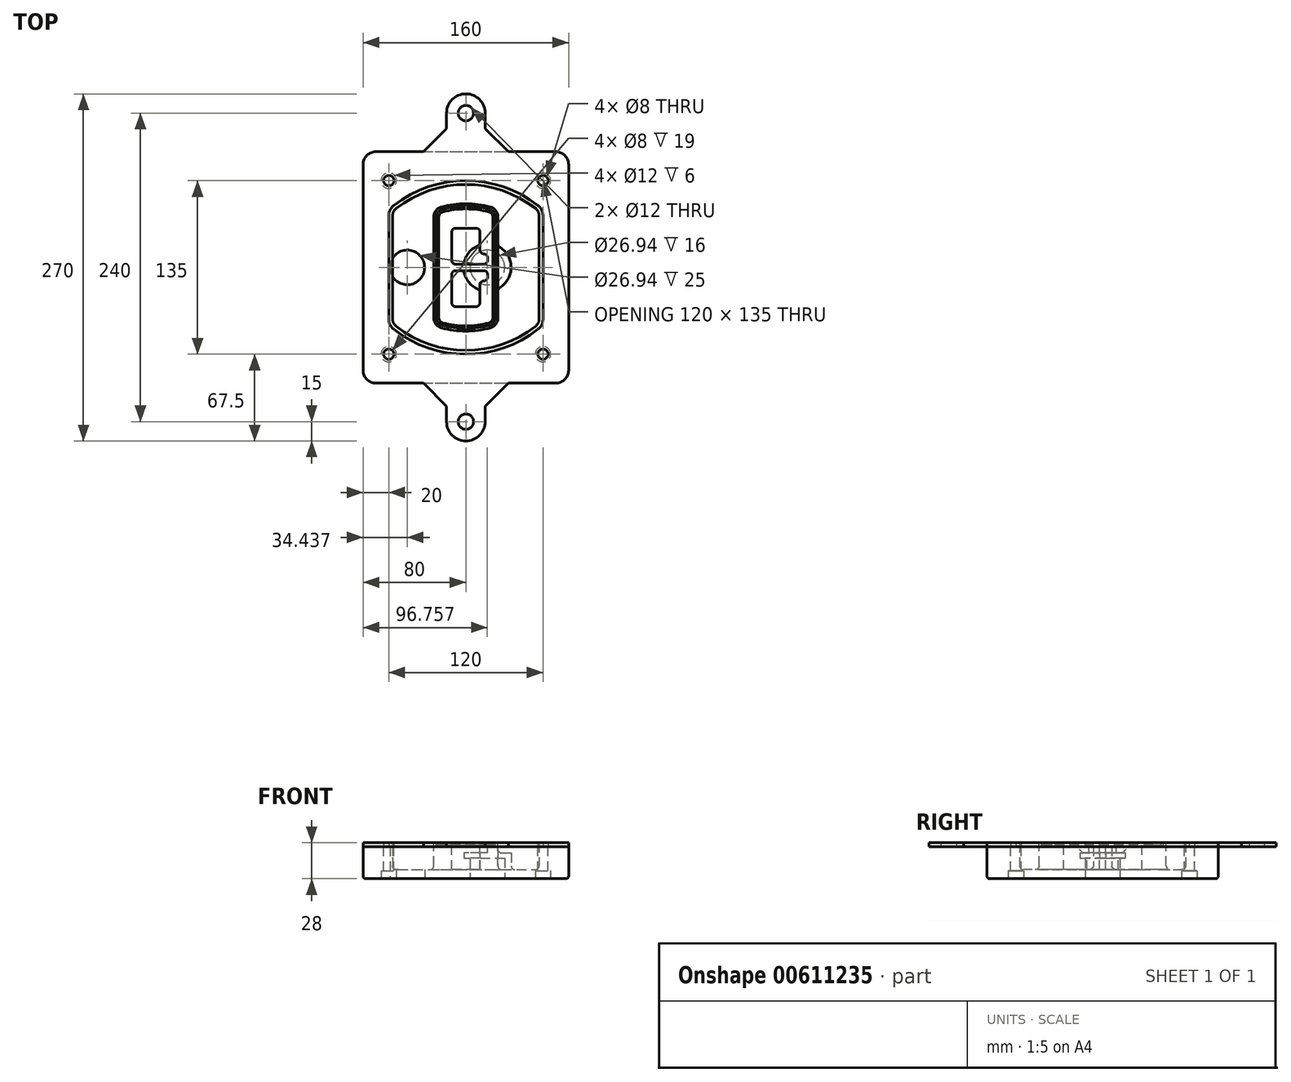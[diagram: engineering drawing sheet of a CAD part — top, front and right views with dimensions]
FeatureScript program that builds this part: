
annotation { "Feature Type Name" : "Feature", "Feature Type Description" : "" }
export const myFeature = defineFeature(function(context is Context, id is Id, definition is map)
    precondition{}
    {
        {
            var Q0;
            Q0=qCreatedBy(makeId("Top.planeOp"),FACE);
            var sketch = newSketch(context, id + "F0", { "sketchPlane" : qUnion([Q0])});
            skPoint(sketch, "E0.rect.middle", {"position": v(0, 0) * mm});
            skLineSegment(sketch, "E1.bottom", {"start": v(-70, -90) * mm, "end": v(70, -90) * mm});
            skLineSegment(sketch, "E1.top", {"start": v(-70, 90) * mm, "end": v(70, 90) * mm});
            skLineSegment(sketch, "E1.left", {"start": v(-80, -80) * mm, "end": v(-80, 80) * mm});
            skLineSegment(sketch, "E1.right", {"start": v(80, -80) * mm, "end": v(80, 80) * mm});
            skLineSegment(sketch, "E2", {"start": v(-80, 90) * mm, "end": v(80, -90) * mm, "construction": true});
            skLineSegment(sketch, "E3", {"start": v(80, 90) * mm, "end": v(-80, -90) * mm, "construction": true});
            skCircle(sketch, "E4", {"center": v(-60, 67.5) * mm, "radius": 4 * mm});
            skCircle(sketch, "E5", {"center": v(60, 67.5) * mm, "radius": 4 * mm});
            skCircle(sketch, "E6", {"center": v(60, -67.5) * mm, "radius": 4 * mm});
            skCircle(sketch, "E7", {"center": v(-60, -67.5) * mm, "radius": 4 * mm});
            skLineSegment(sketch, "E8", {"start": v(-60, 67.5) * mm, "end": v(60, 67.5) * mm, "construction": true});
            skLineSegment(sketch, "E9", {"start": v(60, 67.5) * mm, "end": v(60, -67.5) * mm, "construction": true});
            skLineSegment(sketch, "E10", {"start": v(60, -67.5) * mm, "end": v(-60, -67.5) * mm, "construction": true});
            skLineSegment(sketch, "E11", {"start": v(-60, -67.5) * mm, "end": v(-60, 67.5) * mm, "construction": true});
            skLineSegment(sketch, "E12", {"start": v(-60, 40.3) * mm, "end": v(-60, -40.3) * mm});
            skLineSegment(sketch, "E13", {"start": v(60, 40.3) * mm, "end": v(60, -40.3) * mm});
            skArc(sketch, "E14", {"start": v(56.15, 48.18) * mm, "mid": v(0, 67.5) * mm, "end": v(-56.15, 48.18) * mm});
            skArc(sketch, "E15", {"start": v(-56.15, -48.18) * mm, "mid": v(0, -67.5) * mm, "end": v(56.15, -48.18) * mm});
            skLineSegment(sketch, "E16", {"start": v(-60, 0) * mm, "end": v(60, 0) * mm, "construction": true});
            skPoint(sketch, "E17.visualSharp", {"position": v(-60, -45) * mm});
            skArc(sketch, "E17.filletArc", {"start": v(-60, -40.3) * mm, "mid": v(-58.99, -44.68) * mm, "end": v(-56.15, -48.18) * mm});
            skPoint(sketch, "E18.visualSharp", {"position": v(-60, 45) * mm});
            skArc(sketch, "E18.filletArc", {"start": v(-56.15, 48.18) * mm, "mid": v(-58.99, 44.68) * mm, "end": v(-60, 40.3) * mm});
            skPoint(sketch, "E19.visualSharp", {"position": v(60, 45) * mm});
            skArc(sketch, "E19.filletArc", {"start": v(60, 40.3) * mm, "mid": v(58.99, 44.68) * mm, "end": v(56.15, 48.18) * mm});
            skPoint(sketch, "E20.visualSharp", {"position": v(60, -45) * mm});
            skArc(sketch, "E20.filletArc", {"start": v(56.15, -48.18) * mm, "mid": v(58.99, -44.68) * mm, "end": v(60, -40.3) * mm});
            skPoint(sketch, "E21.visualSharp", {"position": v(-80, 90) * mm});
            skArc(sketch, "E21.filletArc", {"start": v(-70, 90) * mm, "mid": v(-77.07, 87.07) * mm, "end": v(-80, 80) * mm});
            skPoint(sketch, "E22.visualSharp", {"position": v(80, 90) * mm});
            skArc(sketch, "E22.filletArc", {"start": v(80, 80) * mm, "mid": v(77.07, 87.07) * mm, "end": v(70, 90) * mm});
            skPoint(sketch, "E23.visualSharp", {"position": v(80, -90) * mm});
            skArc(sketch, "E23.filletArc", {"start": v(70, -90) * mm, "mid": v(77.07, -87.07) * mm, "end": v(80, -80) * mm});
            skPoint(sketch, "E24.visualSharp", {"position": v(-80, -90) * mm});
            skArc(sketch, "E24.filletArc", {"start": v(-80, -80) * mm, "mid": v(-77.07, -87.07) * mm, "end": v(-70, -90) * mm});
            skArc(sketch, "E25.0", {"start": v(57, 40.3) * mm, "mid": v(56.3, 43.36) * mm, "end": v(54.3, 45.81) * mm});
            skLineSegment(sketch, "E25.1", {"start": v(57, 40.3) * mm, "end": v(57, -40.3) * mm});
            skArc(sketch, "E25.2", {"start": v(54.3, -45.81) * mm, "mid": v(56.3, -43.36) * mm, "end": v(57, -40.3) * mm});
            skArc(sketch, "E25.3", {"start": v(-54.3, -45.81) * mm, "mid": v(0, -64.5) * mm, "end": v(54.3, -45.81) * mm});
            skArc(sketch, "E25.4", {"start": v(-57, -40.3) * mm, "mid": v(-56.3, -43.36) * mm, "end": v(-54.3, -45.81) * mm});
            skArc(sketch, "E25.5", {"start": v(54.3, 45.81) * mm, "mid": v(0, 64.5) * mm, "end": v(-54.3, 45.81) * mm});
            skLineSegment(sketch, "E25.6", {"start": v(-57, 40.3) * mm, "end": v(-57, -40.3) * mm});
            skArc(sketch, "E25.7", {"start": v(-54.3, 45.81) * mm, "mid": v(-56.3, 43.36) * mm, "end": v(-57, 40.3) * mm});
            skArc(sketch, "E26.0", {"start": v(-58.62, 51.33) * mm, "mid": v(-62.58, 46.43) * mm, "end": v(-64, 40.3) * mm});
            skArc(sketch, "E26.1", {"start": v(58.62, 51.33) * mm, "mid": v(0, 71.5) * mm, "end": v(-58.62, 51.33) * mm});
            skArc(sketch, "E26.2", {"start": v(64, 40.3) * mm, "mid": v(62.58, 46.43) * mm, "end": v(58.62, 51.33) * mm});
            skLineSegment(sketch, "E26.3", {"start": v(64, 40.3) * mm, "end": v(64, -40.3) * mm});
            skArc(sketch, "E26.4", {"start": v(58.62, -51.33) * mm, "mid": v(62.58, -46.43) * mm, "end": v(64, -40.3) * mm});
            skLineSegment(sketch, "E26.5", {"start": v(-64, 40.3) * mm, "end": v(-64, -40.3) * mm});
            skArc(sketch, "E26.6", {"start": v(-58.62, -51.33) * mm, "mid": v(0, -71.5) * mm, "end": v(58.62, -51.33) * mm});
            skArc(sketch, "E26.7", {"start": v(-64, -40.3) * mm, "mid": v(-62.58, -46.43) * mm, "end": v(-58.62, -51.33) * mm});
            skSolve(sketch);
        }
        {
            var Q0;
            Q0=makeQuery(id+"F0.imprint","IMPRINT",FACE,{"disambiguationData":[TD([[makeQuery(id+"F0.imprint","IMPRINT",EDGE,{"derivedFrom":sQuery(id+"F0.wireOp",EDGE,"E1.bottom")}),1.0]])]});
            var Q1;
            Q1=makeQuery(id+"F0.imprint","IMPRINT",FACE,{"disambiguationData":[TD([[makeQuery(id+"F0.imprint","IMPRINT",EDGE,{"derivedFrom":sQuery(id+"F0.wireOp",EDGE,"E12")}),1.0]])]});
            var Q2;
            Q2=makeQuery(id+"F0.imprint","IMPRINT",FACE,{"disambiguationData":[TD([[makeQuery(id+"F0.imprint","IMPRINT",EDGE,{"derivedFrom":sQuery(id+"F0.wireOp",EDGE,"E25.0")}),1.0]])]});
            var Q3;
            Q3=makeQuery(id+"F0.imprint","IMPRINT",FACE,{"disambiguationData":[TD([[makeQuery(id+"F0.imprint","IMPRINT",EDGE,{"derivedFrom":sQuery(id+"F0.wireOp",EDGE,"E12")}),-1.0]])]});
            extrude(context, id + "F1", {"entities" : qUnion([Q0, Q1, Q2, Q3]), "oppositeDirection" : true, "depth" : 25 * mm});
        }
        {
            var Q0;
            Q0=makeQuery(id+"F0.imprint","IMPRINT",FACE,{"disambiguationData":[TD([[makeQuery(id+"F0.imprint","IMPRINT",EDGE,{"derivedFrom":sQuery(id+"F0.wireOp",EDGE,"E12")}),1.0]])]});
            extrude(context, id + "F2", {"entities" : qUnion([Q0]), "operationType" : NewBodyOperationType.ADD, "depth" : 3 * mm});
        }
        {
            var Q0;
            Q0=makeQuery(id+"F0.imprint","IMPRINT",FACE,{"disambiguationData":[TD([[makeQuery(id+"F0.imprint","IMPRINT",EDGE,{"derivedFrom":sQuery(id+"F0.wireOp",EDGE,"E25.0")}),1.0]])]});
            extrude(context, id + "F3", {"entities" : qUnion([Q0]), "operationType" : NewBodyOperationType.REMOVE, "oppositeDirection" : true, "depth" : 18 * mm});
        }
        {
            var Q0;
            Q0=makeQuery(id+"F2.opExtrude","CAP_FACE",FACE,{"disambiguationData":[OSD([sQuery(id+"F0.wireOp",EDGE,"E12"),sQuery(id+"F0.wireOp",EDGE,"E13"),sQuery(id+"F0.wireOp",EDGE,"E14"),sQuery(id+"F0.wireOp",EDGE,"E15"),sQuery(id+"F0.wireOp",EDGE,"E17.filletArc"),sQuery(id+"F0.wireOp",EDGE,"E18.filletArc"),sQuery(id+"F0.wireOp",EDGE,"E19.filletArc"),sQuery(id+"F0.wireOp",EDGE,"E20.filletArc"),sQuery(id+"F0.wireOp",EDGE,"E25.0"),sQuery(id+"F0.wireOp",EDGE,"E25.1"),sQuery(id+"F0.wireOp",EDGE,"E25.2"),sQuery(id+"F0.wireOp",EDGE,"E25.3"),sQuery(id+"F0.wireOp",EDGE,"E25.4"),sQuery(id+"F0.wireOp",EDGE,"E25.5"),sQuery(id+"F0.wireOp",EDGE,"E25.6"),sQuery(id+"F0.wireOp",EDGE,"E25.7")])],"isStart":false});
            var sketch = newSketch(context, id + "F4", { "sketchPlane" : qUnion([Q0])});
            skArc(sketch, "E27.0", {"start": v(-19.08, -46.97) * mm, "mid": v(0, -49.5) * mm, "end": v(19.08, -46.97) * mm});
            skArc(sketch, "E28.0", {"start": v(19.08, 46.97) * mm, "mid": v(0, 49.5) * mm, "end": v(-19.08, 46.97) * mm});
            skLineSegment(sketch, "E29", {"start": v(-25, 39.25) * mm, "end": v(-25, -39.25) * mm});
            skLineSegment(sketch, "E30", {"start": v(25, 39.25) * mm, "end": v(25, -39.25) * mm});
            skLineSegment(sketch, "E31", {"start": v(-25, 45.1) * mm, "end": v(25, 45.1) * mm, "construction": true});
            skLineSegment(sketch, "E32", {"start": v(-25, -45.1) * mm, "end": v(25, -45.1) * mm, "construction": true});
            skPoint(sketch, "E33.visualSharp", {"position": v(-25, 45.1) * mm});
            skArc(sketch, "E33.filletArc", {"start": v(-19.08, 46.97) * mm, "mid": v(-23.35, 44.11) * mm, "end": v(-25, 39.25) * mm});
            skPoint(sketch, "E34.visualSharp", {"position": v(25, 45.1) * mm});
            skArc(sketch, "E34.filletArc", {"start": v(25, 39.25) * mm, "mid": v(23.35, 44.11) * mm, "end": v(19.08, 46.97) * mm});
            skPoint(sketch, "E35.visualSharp", {"position": v(25, -45.1) * mm});
            skArc(sketch, "E35.filletArc", {"start": v(19.08, -46.97) * mm, "mid": v(23.35, -44.11) * mm, "end": v(25, -39.25) * mm});
            skPoint(sketch, "E36.visualSharp", {"position": v(-25, -45.1) * mm});
            skArc(sketch, "E36.filletArc", {"start": v(-25, -39.25) * mm, "mid": v(-23.35, -44.11) * mm, "end": v(-19.08, -46.97) * mm});
            skArc(sketch, "E37.0", {"start": v(54.3, 45.81) * mm, "mid": v(0, 64.5) * mm, "end": v(-54.3, 45.81) * mm});
            skArc(sketch, "E37.1", {"start": v(-54.3, 45.81) * mm, "mid": v(-56.3, 43.36) * mm, "end": v(-57, 40.3) * mm});
            skLineSegment(sketch, "E37.2", {"start": v(-57, 40.3) * mm, "end": v(-57, -40.3) * mm});
            skArc(sketch, "E37.3", {"start": v(-57, -40.3) * mm, "mid": v(-56.3, -43.36) * mm, "end": v(-54.3, -45.81) * mm});
            skArc(sketch, "E37.4", {"start": v(-54.3, -45.81) * mm, "mid": v(0, -64.5) * mm, "end": v(54.3, -45.81) * mm});
            skArc(sketch, "E37.5", {"start": v(54.3, -45.81) * mm, "mid": v(56.3, -43.36) * mm, "end": v(57, -40.3) * mm});
            skLineSegment(sketch, "E37.6", {"start": v(57, 40.3) * mm, "end": v(57, -40.3) * mm});
            skArc(sketch, "E37.7", {"start": v(57, 40.3) * mm, "mid": v(56.3, 43.36) * mm, "end": v(54.3, 45.81) * mm});
            skLineSegment(sketch, "E38.0", {"start": v(23, 39.25) * mm, "end": v(23, -39.25) * mm});
            skArc(sketch, "E38.1", {"start": v(18.56, -45.04) * mm, "mid": v(21.76, -42.9) * mm, "end": v(23, -39.25) * mm});
            skArc(sketch, "E38.2", {"start": v(-18.56, -45.04) * mm, "mid": v(0, -47.5) * mm, "end": v(18.56, -45.04) * mm});
            skArc(sketch, "E38.3", {"start": v(-23, -39.25) * mm, "mid": v(-21.76, -42.9) * mm, "end": v(-18.56, -45.04) * mm});
            skLineSegment(sketch, "E38.4", {"start": v(-23, 39.25) * mm, "end": v(-23, -39.25) * mm});
            skArc(sketch, "E38.5", {"start": v(23, 39.25) * mm, "mid": v(21.76, 42.9) * mm, "end": v(18.56, 45.04) * mm});
            skArc(sketch, "E38.6", {"start": v(-18.56, 45.04) * mm, "mid": v(-21.76, 42.9) * mm, "end": v(-23, 39.25) * mm});
            skArc(sketch, "E38.7", {"start": v(18.56, 45.04) * mm, "mid": v(0, 47.5) * mm, "end": v(-18.56, 45.04) * mm});
            skArc(sketch, "E39.0", {"start": v(21, 39.25) * mm, "mid": v(20.18, 41.68) * mm, "end": v(18.04, 43.1) * mm});
            skLineSegment(sketch, "E39.1", {"start": v(21, 39.25) * mm, "end": v(21, -39.25) * mm});
            skArc(sketch, "E39.2", {"start": v(18.04, -43.1) * mm, "mid": v(20.18, -41.68) * mm, "end": v(21, -39.25) * mm});
            skArc(sketch, "E39.3", {"start": v(-18.04, -43.1) * mm, "mid": v(0, -45.5) * mm, "end": v(18.04, -43.1) * mm});
            skArc(sketch, "E39.4", {"start": v(-21, -39.25) * mm, "mid": v(-20.18, -41.68) * mm, "end": v(-18.04, -43.1) * mm});
            skArc(sketch, "E39.5", {"start": v(18.04, 43.1) * mm, "mid": v(0, 45.5) * mm, "end": v(-18.04, 43.1) * mm});
            skLineSegment(sketch, "E39.6", {"start": v(-21, 39.25) * mm, "end": v(-21, -39.25) * mm});
            skArc(sketch, "E39.7", {"start": v(-18.04, 43.1) * mm, "mid": v(-20.18, 41.68) * mm, "end": v(-21, 39.25) * mm});
            skLineSegment(sketch, "E40", {"start": v(-25, 0) * mm, "end": v(25, 0) * mm, "construction": true});
            skLineSegment(sketch, "E41", {"start": v(-11, 5.5) * mm, "end": v(-11, 27.5) * mm});
            skLineSegment(sketch, "E42", {"start": v(-8, 30.5) * mm, "end": v(8, 30.5) * mm});
            skLineSegment(sketch, "E43", {"start": v(11, 27.5) * mm, "end": v(11, 13.5) * mm});
            skLineSegment(sketch, "E44", {"start": v(14, 10.5) * mm, "end": v(14, 10.5) * mm});
            skLineSegment(sketch, "E45", {"start": v(17, 7.5) * mm, "end": v(17, 5.5) * mm});
            skLineSegment(sketch, "E46", {"start": v(14, 2.5) * mm, "end": v(-8, 2.5) * mm});
            skPoint(sketch, "E47.visualSharp", {"position": v(-11, 30.5) * mm});
            skArc(sketch, "E47.filletArc", {"start": v(-8, 30.5) * mm, "mid": v(-10.12, 29.62) * mm, "end": v(-11, 27.5) * mm});
            skPoint(sketch, "E48.visualSharp", {"position": v(11, 30.5) * mm});
            skArc(sketch, "E48.filletArc", {"start": v(11, 27.5) * mm, "mid": v(10.12, 29.62) * mm, "end": v(8, 30.5) * mm});
            skPoint(sketch, "E49.visualSharp", {"position": v(11, 10.5) * mm});
            skArc(sketch, "E49.filletArc", {"start": v(11, 13.5) * mm, "mid": v(11.88, 11.38) * mm, "end": v(14, 10.5) * mm});
            skPoint(sketch, "E50.visualSharp", {"position": v(17, 10.5) * mm});
            skArc(sketch, "E50.filletArc", {"start": v(17, 7.5) * mm, "mid": v(16.12, 9.62) * mm, "end": v(14, 10.5) * mm});
            skPoint(sketch, "E51.visualSharp", {"position": v(17, 2.5) * mm});
            skArc(sketch, "E51.filletArc", {"start": v(14, 2.5) * mm, "mid": v(16.12, 3.38) * mm, "end": v(17, 5.5) * mm});
            skPoint(sketch, "E52.visualSharp", {"position": v(-11, 2.5) * mm});
            skArc(sketch, "E52.filletArc", {"start": v(-11, 5.5) * mm, "mid": v(-10.12, 3.38) * mm, "end": v(-8, 2.5) * mm});
            skLineSegment(sketch, "E53.0.MirrorCS", {"start": v(14, -2.5) * mm, "end": v(-8, -2.5) * mm});
            skArc(sketch, "E54.0.MirrorCS", {"start": v(-11, -5.5) * mm, "mid": v(-10.12, -3.38) * mm, "end": v(-8, -2.5) * mm});
            skLineSegment(sketch, "E55.0.MirrorCS", {"start": v(-11, -5.5) * mm, "end": v(-11, -27.5) * mm});
            skArc(sketch, "E56.0.MirrorCS", {"start": v(-8, -30.5) * mm, "mid": v(-10.12, -29.62) * mm, "end": v(-11, -27.5) * mm});
            skLineSegment(sketch, "E57.0.MirrorCS", {"start": v(-8, -30.5) * mm, "end": v(8, -30.5) * mm});
            skArc(sketch, "E58.0.MirrorCS", {"start": v(11, -27.5) * mm, "mid": v(10.12, -29.62) * mm, "end": v(8, -30.5) * mm});
            skLineSegment(sketch, "E59.0.MirrorCS", {"start": v(11, -27.5) * mm, "end": v(11, -13.5) * mm});
            skArc(sketch, "E60.0.MirrorCS", {"start": v(11, -13.5) * mm, "mid": v(11.88, -11.38) * mm, "end": v(14, -10.5) * mm});
            skArc(sketch, "E61.0.MirrorCS", {"start": v(17, -7.5) * mm, "mid": v(16.12, -9.62) * mm, "end": v(14, -10.5) * mm});
            skLineSegment(sketch, "E62.0.MirrorCS", {"start": v(17, -7.5) * mm, "end": v(17, -5.5) * mm});
            skArc(sketch, "E63.0.MirrorCS", {"start": v(14, -2.5) * mm, "mid": v(16.12, -3.38) * mm, "end": v(17, -5.5) * mm});
            skSolve(sketch);
        }
        {
            var Q0;
            Q0=makeQuery(id+"F4.imprint","IMPRINT",FACE,{"disambiguationData":[TD([[makeQuery(id+"F4.imprint","IMPRINT",EDGE,{"derivedFrom":sQuery(id+"F4.wireOp",EDGE,"E27.0")}),1.0]])]});
            var Q1;
            Q1=makeQuery(id+"F4.imprint","IMPRINT",FACE,{"disambiguationData":[TD([[makeQuery(id+"F4.imprint","IMPRINT",EDGE,{"derivedFrom":sQuery(id+"F4.wireOp",EDGE,"E38.0")}),-1.0]])]});
            var Q2;
            Q2=makeQuery(id+"F4.imprint","IMPRINT",FACE,{"disambiguationData":[TD([[makeQuery(id+"F4.imprint","IMPRINT",EDGE,{"derivedFrom":sQuery(id+"F4.wireOp",EDGE,"E39.0")}),1.0]])]});
            extrude(context, id + "F5", {"entities" : qUnion([Q0, Q1, Q2]), "operationType" : NewBodyOperationType.ADD, "endBound" : BoundingType.UP_TO_NEXT, "oppositeDirection" : true, "depth" : 25 * mm});
        }
        {
            var Q0;
            Q0=makeQuery(id+"F4.imprint","IMPRINT",FACE,{"disambiguationData":[TD([[makeQuery(id+"F4.imprint","IMPRINT",EDGE,{"derivedFrom":sQuery(id+"F4.wireOp",EDGE,"E38.0")}),-1.0]])]});
            extrude(context, id + "F6", {"entities" : qUnion([Q0]), "operationType" : NewBodyOperationType.REMOVE, "oppositeDirection" : true, "depth" : 2 * mm});
        }
        {
            var Q0;
            Q0=makeQuery(id+"F1.opExtrude","CAP_FACE",FACE,{"disambiguationData":[OSD([sQuery(id+"F0.wireOp",EDGE,"E1.bottom"),sQuery(id+"F0.wireOp",EDGE,"E1.top"),sQuery(id+"F0.wireOp",EDGE,"E1.left"),sQuery(id+"F0.wireOp",EDGE,"E1.right"),sQuery(id+"F0.wireOp",EDGE,"E4"),sQuery(id+"F0.wireOp",EDGE,"E5"),sQuery(id+"F0.wireOp",EDGE,"E6"),sQuery(id+"F0.wireOp",EDGE,"E7"),sQuery(id+"F0.wireOp",EDGE,"E21.filletArc"),sQuery(id+"F0.wireOp",EDGE,"E22.filletArc"),sQuery(id+"F0.wireOp",EDGE,"E23.filletArc"),sQuery(id+"F0.wireOp",EDGE,"E24.filletArc")])],"isStart":false});
            var sketch = newSketch(context, id + "F7", { "sketchPlane" : qUnion([Q0])});
            skCircle(sketch, "E64", {"center": v(16.76, 0) * mm, "radius": 13.47 * mm});
            skCircle(sketch, "E65", {"center": v(-45.56, 0) * mm, "radius": 13.47 * mm});
            skLineSegment(sketch, "E66", {"start": v(80, 0) * mm, "end": v(-80, 0) * mm});
            skCircle(sketch, "E67", {"center": v(16.76, 0) * mm, "radius": 18.47 * mm});
            skCircle(sketch, "E68", {"center": v(60, -67.5) * mm, "radius": 6 * mm});
            skCircle(sketch, "E69", {"center": v(-60, -67.5) * mm, "radius": 6 * mm});
            skCircle(sketch, "E70", {"center": v(-60, 67.5) * mm, "radius": 6 * mm});
            skCircle(sketch, "E71", {"center": v(60, 67.5) * mm, "radius": 6 * mm});
            skSolve(sketch);
        }
        {
            var Q0;
            {var subQ1=sQuery(id+"F7.wireOp",EDGE,"E66");var subQ4=sQuery(id+"F7.wireOp",EDGE,"E64");var subQ6=makeQuery(id+"F7.imprint","INTERSECT",VERTEX,{"disambiguationData":[OD(0.0)],"derivedFrom":[subQ4,subQ1]});Q0=makeQuery(id+"F7.imprint","IMPRINT",FACE,{"disambiguationData":[TD([[makeQuery(id+"F7.imprint","IMPRINT",EDGE,{"disambiguationData":[TD([[subQ6,-1.0]])],"derivedFrom":subQ4}),-1.0]])]});}
            var Q1;
            {var subQ0=sQuery(id+"F7.wireOp",EDGE,"E66");var subQ1=sQuery(id+"F7.wireOp",EDGE,"E64");var subQ3=makeQuery(id+"F7.imprint","INTERSECT",VERTEX,{"disambiguationData":[OD(0.0)],"derivedFrom":[subQ1,subQ0]});Q1=makeQuery(id+"F7.imprint","IMPRINT",FACE,{"disambiguationData":[TD([[makeQuery(id+"F7.imprint","IMPRINT",EDGE,{"disambiguationData":[TD([[subQ3,-1.0]])],"derivedFrom":subQ1}),1.0]])]});}
            var Q2;
            {var subQ0=sQuery(id+"F7.wireOp",EDGE,"E66");var subQ1=sQuery(id+"F7.wireOp",EDGE,"E64");var subQ3=makeQuery(id+"F7.imprint","INTERSECT",VERTEX,{"disambiguationData":[OD(0.0)],"derivedFrom":[subQ1,subQ0]});Q2=makeQuery(id+"F7.imprint","IMPRINT",FACE,{"disambiguationData":[TD([[makeQuery(id+"F7.imprint","IMPRINT",EDGE,{"disambiguationData":[TD([[subQ3,1.0]])],"derivedFrom":subQ1}),1.0]])]});}
            var Q3;
            {var subQ1=sQuery(id+"F7.wireOp",EDGE,"E66");var subQ4=sQuery(id+"F7.wireOp",EDGE,"E64");var subQ6=makeQuery(id+"F7.imprint","INTERSECT",VERTEX,{"disambiguationData":[OD(0.0)],"derivedFrom":[subQ4,subQ1]});Q3=makeQuery(id+"F7.imprint","IMPRINT",FACE,{"disambiguationData":[TD([[makeQuery(id+"F7.imprint","IMPRINT",EDGE,{"disambiguationData":[TD([[subQ6,1.0]])],"derivedFrom":subQ4}),-1.0]])]});}
            extrude(context, id + "F8", {"entities" : qUnion([Q0, Q1, Q2, Q3]), "operationType" : NewBodyOperationType.ADD, "oppositeDirection" : true, "depth" : 20 * mm});
        }
        {
            var Q0;
            {var subQ0=sQuery(id+"F7.wireOp",EDGE,"E66");var subQ1=sQuery(id+"F7.wireOp",EDGE,"E64");var subQ3=makeQuery(id+"F7.imprint","INTERSECT",VERTEX,{"disambiguationData":[OD(0.0)],"derivedFrom":[subQ1,subQ0]});Q0=makeQuery(id+"F7.imprint","IMPRINT",FACE,{"disambiguationData":[TD([[makeQuery(id+"F7.imprint","IMPRINT",EDGE,{"disambiguationData":[TD([[subQ3,-1.0]])],"derivedFrom":subQ1}),1.0]])]});}
            var Q1;
            {var subQ0=sQuery(id+"F7.wireOp",EDGE,"E66");var subQ1=sQuery(id+"F7.wireOp",EDGE,"E64");var subQ3=makeQuery(id+"F7.imprint","INTERSECT",VERTEX,{"disambiguationData":[OD(0.0)],"derivedFrom":[subQ1,subQ0]});Q1=makeQuery(id+"F7.imprint","IMPRINT",FACE,{"disambiguationData":[TD([[makeQuery(id+"F7.imprint","IMPRINT",EDGE,{"disambiguationData":[TD([[subQ3,1.0]])],"derivedFrom":subQ1}),1.0]])]});}
            extrude(context, id + "F9", {"entities" : qUnion([Q0, Q1]), "operationType" : NewBodyOperationType.REMOVE, "oppositeDirection" : true, "depth" : 16 * mm});
        }
        {
            var Q0;
            {var subQ0=sQuery(id+"F7.wireOp",EDGE,"E66");var subQ1=sQuery(id+"F7.wireOp",EDGE,"E65");var subQ3=makeQuery(id+"F7.imprint","INTERSECT",VERTEX,{"disambiguationData":[OD(0.0)],"derivedFrom":[subQ1,subQ0]});Q0=makeQuery(id+"F7.imprint","IMPRINT",FACE,{"disambiguationData":[TD([[makeQuery(id+"F7.imprint","IMPRINT",EDGE,{"disambiguationData":[TD([[subQ3,-1.0]])],"derivedFrom":subQ1}),1.0]])]});}
            var Q1;
            {var subQ0=sQuery(id+"F7.wireOp",EDGE,"E66");var subQ1=sQuery(id+"F7.wireOp",EDGE,"E65");var subQ3=makeQuery(id+"F7.imprint","INTERSECT",VERTEX,{"disambiguationData":[OD(0.0)],"derivedFrom":[subQ1,subQ0]});Q1=makeQuery(id+"F7.imprint","IMPRINT",FACE,{"disambiguationData":[TD([[makeQuery(id+"F7.imprint","IMPRINT",EDGE,{"disambiguationData":[TD([[subQ3,1.0]])],"derivedFrom":subQ1}),1.0]])]});}
            extrude(context, id + "F10", {"entities" : qUnion([Q0, Q1]), "operationType" : NewBodyOperationType.REMOVE, "oppositeDirection" : true, "depth" : 25 * mm});
        }
        {
            var Q0;
            Q0=makeQuery(id+"F7.imprint","IMPRINT",FACE,{"disambiguationData":[TD([[makeQuery(id+"F7.imprint","IMPRINT",EDGE,{"derivedFrom":sQuery(id+"F7.wireOp",EDGE,"E68")}),1.0]])]});
            var Q1;
            Q1=makeQuery(id+"F7.imprint","IMPRINT",FACE,{"disambiguationData":[TD([[makeQuery(id+"F7.imprint","IMPRINT",EDGE,{"derivedFrom":makeQuery(id+"F1.opExtrude","CAP_EDGE",EDGE,{"disambiguationData":[OSD([sQuery(id+"F0.wireOp",EDGE,"E5")])],"isStart":false})}),-1.0]])]});
            var Q2;
            Q2=makeQuery(id+"F7.imprint","IMPRINT",FACE,{"disambiguationData":[TD([[makeQuery(id+"F7.imprint","IMPRINT",EDGE,{"derivedFrom":sQuery(id+"F7.wireOp",EDGE,"E69")}),1.0]])]});
            var Q3;
            Q3=makeQuery(id+"F7.imprint","IMPRINT",FACE,{"disambiguationData":[TD([[makeQuery(id+"F7.imprint","IMPRINT",EDGE,{"derivedFrom":makeQuery(id+"F1.opExtrude","CAP_EDGE",EDGE,{"disambiguationData":[OSD([sQuery(id+"F0.wireOp",EDGE,"E4")])],"isStart":false})}),-1.0]])]});
            var Q4;
            Q4=makeQuery(id+"F7.imprint","IMPRINT",FACE,{"disambiguationData":[TD([[makeQuery(id+"F7.imprint","IMPRINT",EDGE,{"derivedFrom":sQuery(id+"F7.wireOp",EDGE,"E70")}),1.0]])]});
            var Q5;
            Q5=makeQuery(id+"F7.imprint","IMPRINT",FACE,{"disambiguationData":[TD([[makeQuery(id+"F7.imprint","IMPRINT",EDGE,{"derivedFrom":makeQuery(id+"F1.opExtrude","CAP_EDGE",EDGE,{"disambiguationData":[OSD([sQuery(id+"F0.wireOp",EDGE,"E7")])],"isStart":false})}),-1.0]])]});
            var Q6;
            Q6=makeQuery(id+"F7.imprint","IMPRINT",FACE,{"disambiguationData":[TD([[makeQuery(id+"F7.imprint","IMPRINT",EDGE,{"derivedFrom":sQuery(id+"F7.wireOp",EDGE,"E71")}),1.0]])]});
            var Q7;
            Q7=makeQuery(id+"F7.imprint","IMPRINT",FACE,{"disambiguationData":[TD([[makeQuery(id+"F7.imprint","IMPRINT",EDGE,{"derivedFrom":makeQuery(id+"F1.opExtrude","CAP_EDGE",EDGE,{"disambiguationData":[OSD([sQuery(id+"F0.wireOp",EDGE,"E6")])],"isStart":false})}),-1.0]])]});
            extrude(context, id + "F11", {"entities" : qUnion([Q0, Q1, Q2, Q3, Q4, Q5, Q6, Q7]), "operationType" : NewBodyOperationType.REMOVE, "oppositeDirection" : true, "depth" : 6 * mm});
        }
        {
            var Q0;
            Q0=makeQuery(id+"F9.boolean.opBoolean","COPY",FACE,{"derivedFrom":makeQuery(id+"F9.opExtrude","CAP_FACE",FACE,{"disambiguationData":[OSD([sQuery(id+"F7.wireOp",EDGE,"E64")])],"isStart":false})});
            var sketch = newSketch(context, id + "F12", { "sketchPlane" : qUnion([Q0])});
            skArc(sketch, "E72.0", {"start": v(11, 17.55) * mm, "mid": v(2.57, 11.82) * mm, "end": v(-1.54, 2.5) * mm});
            skArc(sketch, "E72.1", {"start": v(-1.54, -2.5) * mm, "mid": v(2.57, -11.82) * mm, "end": v(11, -17.55) * mm});
            skLineSegment(sketch, "E73", {"start": v(-1.54, -2.5) * mm, "end": v(14, -2.5) * mm});
            skLineSegment(sketch, "E74.0", {"start": v(14, 2.5) * mm, "end": v(-1.54, 2.5) * mm});
            skArc(sketch, "E74.1", {"start": v(14, 2.5) * mm, "mid": v(16.12, 3.38) * mm, "end": v(17, 5.5) * mm});
            skLineSegment(sketch, "E74.2", {"start": v(17, 7.5) * mm, "end": v(17, 5.5) * mm});
            skArc(sketch, "E74.3", {"start": v(17, 7.5) * mm, "mid": v(16.12, 9.62) * mm, "end": v(14, 10.5) * mm});
            skArc(sketch, "E74.4", {"start": v(11, 13.5) * mm, "mid": v(11.88, 11.38) * mm, "end": v(14, 10.5) * mm});
            skLineSegment(sketch, "E74.5", {"start": v(11, 17.55) * mm, "end": v(11, 13.5) * mm});
            skLineSegment(sketch, "E74.7", {"start": v(14, -2.5) * mm, "end": v(-1.54, -2.5) * mm});
            skArc(sketch, "E74.8", {"start": v(14, -2.5) * mm, "mid": v(16.12, -3.38) * mm, "end": v(17, -5.5) * mm});
            skLineSegment(sketch, "E74.9", {"start": v(17, -7.5) * mm, "end": v(17, -5.5) * mm});
            skArc(sketch, "E74.10", {"start": v(17, -7.5) * mm, "mid": v(16.12, -9.62) * mm, "end": v(14, -10.5) * mm});
            skArc(sketch, "E74.11", {"start": v(11, -13.5) * mm, "mid": v(11.88, -11.38) * mm, "end": v(14, -10.5) * mm});
            skLineSegment(sketch, "E74.12", {"start": v(11, -17.55) * mm, "end": v(11, -13.5) * mm});
            skPoint(sketch, "E75.orphan", {"position": v(11, -27.5) * mm});
            skPoint(sketch, "E76.orphan", {"position": v(-8, -2.5) * mm});
            skPoint(sketch, "E77.orphan", {"position": v(-8, 2.5) * mm});
            skPoint(sketch, "E78.orphan", {"position": v(11, 27.5) * mm});
            skSolve(sketch);
        }
        {
            var Q0;
            {var subQ7=sQuery(id+"F12.wireOp",EDGE,"E72.0");var subQ14=sQuery(id+"F12.wireOp",EDGE,"E72.1");var subQ16=sQuery(id+"F12.wireOp",EDGE,"E74.1");var subQ18=sQuery(id+"F12.wireOp",EDGE,"E74.8");Q0=qUnion([makeQuery(id+"F12.imprint","IMPRINT",FACE,{"disambiguationData":[TD([[makeQuery(id+"F12.imprint","IMPRINT",EDGE,{"derivedFrom":subQ7}),1.0]])]}),makeQuery(id+"F12.imprint","IMPRINT",FACE,{"disambiguationData":[TD([[makeQuery(id+"F12.imprint","IMPRINT",EDGE,{"derivedFrom":subQ14}),1.0]])]}),makeQuery(id+"F12.imprint","IMPRINT",FACE,{"disambiguationData":[TD([[makeQuery(id+"F12.imprint","IMPRINT",EDGE,{"derivedFrom":subQ16}),1.0]])]}),makeQuery(id+"F12.imprint","IMPRINT",FACE,{"disambiguationData":[TD([[makeQuery(id+"F12.imprint","IMPRINT",EDGE,{"derivedFrom":subQ18}),-1.0]])]})]);}
            var Q1;
            Q1=makeQuery(id+"F5.boolean.opBoolean","SPLIT",FACE,{"disambiguationData":[TD([makeQuery(id+"F5.opExtrude","SWEPT_FACE",FACE,{"disambiguationData":[OSD([sQuery(id+"F4.wireOp",EDGE,"E41")])]})])],"derivedFrom":makeQuery(id+"F3.boolean.opBoolean","COPY",FACE,{"derivedFrom":makeQuery(id+"F3.opExtrude","CAP_FACE",FACE,{"disambiguationData":[OSD([sQuery(id+"F0.wireOp",EDGE,"E25.0"),sQuery(id+"F0.wireOp",EDGE,"E25.1"),sQuery(id+"F0.wireOp",EDGE,"E25.2"),sQuery(id+"F0.wireOp",EDGE,"E25.3"),sQuery(id+"F0.wireOp",EDGE,"E25.4"),sQuery(id+"F0.wireOp",EDGE,"E25.5"),sQuery(id+"F0.wireOp",EDGE,"E25.6"),sQuery(id+"F0.wireOp",EDGE,"E25.7")])],"isStart":false})})});
            extrude(context, id + "F13", {"entities" : qUnion([Q0]), "operationType" : NewBodyOperationType.REMOVE, "endBound" : BoundingType.UP_TO_SURFACE, "endBoundEntityFace" : qUnion([Q1]), "depth" : 25 * mm});
        }
        {
            var Q0;
            Q0=makeQuery(id+"F3.boolean.opBoolean","COPY",EDGE,{"derivedFrom":makeQuery(id+"F3.opExtrude","CAP_EDGE",EDGE,{"disambiguationData":[OSD([sQuery(id+"F0.wireOp",EDGE,"E25.6")])],"isStart":false})});
            var Q1;
            Q1=makeQuery(id+"F8.boolean.opBoolean","INTERSECT",EDGE,{"derivedFrom":[makeQuery(id+"F5.opExtrude","SWEPT_FACE",FACE,{"disambiguationData":[OSD([sQuery(id+"F4.wireOp",EDGE,"E30")])]}),makeQuery(id+"F8.opExtrude","CAP_FACE",FACE,{"disambiguationData":[OSD([sQuery(id+"F7.wireOp",EDGE,"E67")])],"isStart":false})]});
            var Q2;
            Q2=makeQuery(id+"F8.boolean.opBoolean","INTERSECT",EDGE,{"disambiguationData":[OD(1.0)],"derivedFrom":[makeQuery(id+"F5.opExtrude","SWEPT_FACE",FACE,{"disambiguationData":[OSD([sQuery(id+"F4.wireOp",EDGE,"E30")])]}),makeQuery(id+"F8.opExtrude","SWEPT_FACE",FACE,{"disambiguationData":[OSD([sQuery(id+"F7.wireOp",EDGE,"E67")])]})]});
            var Q3;
            {var subQ0=sQuery(id+"F4.wireOp",EDGE,"E30");Q3=makeQuery(id+"F8.boolean.opBoolean","SPLIT",EDGE,{"disambiguationData":[TD([makeQuery(id+"F5.opExtrude","SWEPT_FACE",FACE,{"disambiguationData":[OSD([sQuery(id+"F4.wireOp",EDGE,"E35.filletArc")])]})])],"derivedFrom":makeQuery(id+"F5.opExtrude","CAP_EDGE",EDGE,{"disambiguationData":[OSD([subQ0])],"isStart":false})});}
            var Q4;
            {var subQ0=sQuery(id+"F0.wireOp",EDGE,"E25.7");var subQ1=sQuery(id+"F0.wireOp",EDGE,"E25.1");var subQ2=sQuery(id+"F0.wireOp",EDGE,"E25.6");var subQ3=sQuery(id+"F0.wireOp",EDGE,"E25.5");var subQ4=sQuery(id+"F0.wireOp",EDGE,"E25.4");var subQ5=sQuery(id+"F0.wireOp",EDGE,"E25.0");var subQ6=sQuery(id+"F0.wireOp",EDGE,"E25.2");var subQ7=sQuery(id+"F0.wireOp",EDGE,"E25.3");Q4=makeQuery(id+"F8.boolean.opBoolean","INTERSECT",EDGE,{"derivedFrom":[makeQuery(id+"F5.boolean.opBoolean","SPLIT",FACE,{"disambiguationData":[TD([makeQuery(id+"F2.opExtrude","SWEPT_FACE",FACE,{"disambiguationData":[OSD([subQ5])]})])],"derivedFrom":makeQuery(id+"F3.boolean.opBoolean","COPY",FACE,{"derivedFrom":makeQuery(id+"F3.opExtrude","CAP_FACE",FACE,{"disambiguationData":[OSD([subQ5,subQ1,subQ6,subQ7,subQ4,subQ3,subQ2,subQ0])],"isStart":false})})}),makeQuery(id+"F8.opExtrude","SWEPT_FACE",FACE,{"disambiguationData":[OSD([sQuery(id+"F7.wireOp",EDGE,"E67")])]})]});}
            var Q5;
            Q5=makeQuery(id+"F8.boolean.opBoolean","INTERSECT",EDGE,{"disambiguationData":[OD(0.0)],"derivedFrom":[makeQuery(id+"F5.opExtrude","SWEPT_FACE",FACE,{"disambiguationData":[OSD([sQuery(id+"F4.wireOp",EDGE,"E30")])]}),makeQuery(id+"F8.opExtrude","SWEPT_FACE",FACE,{"disambiguationData":[OSD([sQuery(id+"F7.wireOp",EDGE,"E67")])]})]});
            fillet(context, id + "F14", {"entities" : qUnion([Q0, Q1, Q2, Q3, Q4, Q5]), "radius" : 3 * mm, "tangentPropagation" : true, "allowEdgeOverflow" : false});
        }
        {
            var Q0;
            Q0=makeQuery(id+"F1.opExtrude","CAP_EDGE",EDGE,{"disambiguationData":[OSD([sQuery(id+"F0.wireOp",EDGE,"E1.bottom")])],"isStart":false});
            fillet(context, id + "F15", {"entities" : qUnion([Q0]), "radius" : 2 * mm, "tangentPropagation" : true, "allowEdgeOverflow" : false});
        }
        {
            var Q0;
            {var subQ0=sQuery(id+"F0.wireOp",EDGE,"E21.filletArc");var subQ1=sQuery(id+"F0.wireOp",EDGE,"E7");var subQ2=sQuery(id+"F0.wireOp",EDGE,"E6");var subQ3=sQuery(id+"F0.wireOp",EDGE,"E5");var subQ4=sQuery(id+"F0.wireOp",EDGE,"E4");var subQ5=sQuery(id+"F0.wireOp",EDGE,"E22.filletArc");var subQ6=sQuery(id+"F0.wireOp",EDGE,"E1.bottom");var subQ7=sQuery(id+"F0.wireOp",EDGE,"E1.right");var subQ8=sQuery(id+"F0.wireOp",EDGE,"E1.top");var subQ9=sQuery(id+"F0.wireOp",EDGE,"E1.left");var subQ10=sQuery(id+"F0.wireOp",EDGE,"E23.filletArc");var subQ11=sQuery(id+"F0.wireOp",EDGE,"E24.filletArc");Q0=makeQuery(id+"F2.boolean.opBoolean","SPLIT",FACE,{"disambiguationData":[TD([makeQuery(id+"F1.opExtrude","SWEPT_FACE",FACE,{"disambiguationData":[OSD([subQ6])]})])],"derivedFrom":makeQuery(id+"F1.opExtrude","CAP_FACE",FACE,{"disambiguationData":[OSD([subQ6,subQ8,subQ9,subQ7,subQ4,subQ3,subQ2,subQ1,subQ0,subQ5,subQ10,subQ11])],"isStart":true})});}
            var sketch = newSketch(context, id + "F16", { "sketchPlane" : qUnion([Q0])});
            skLineSegment(sketch, "E79.0", {"start": v(-80, -80) * mm, "end": v(-80, 80) * mm});
            skLineSegment(sketch, "E79.1", {"start": v(-70, -90) * mm, "end": v(70, -90) * mm});
            skArc(sketch, "E79.2", {"start": v(70, -90) * mm, "mid": v(77.07, -87.07) * mm, "end": v(80, -80) * mm});
            skArc(sketch, "E79.3", {"start": v(-80, -80) * mm, "mid": v(-77.07, -87.07) * mm, "end": v(-70, -90) * mm});
            skLineSegment(sketch, "E79.4", {"start": v(80, -80) * mm, "end": v(80, 80) * mm});
            skArc(sketch, "E79.5", {"start": v(80, 80) * mm, "mid": v(77.07, 87.07) * mm, "end": v(70, 90) * mm});
            skLineSegment(sketch, "E79.6", {"start": v(-70, 90) * mm, "end": v(70, 90) * mm});
            skArc(sketch, "E79.7", {"start": v(-70, 90) * mm, "mid": v(-77.07, 87.07) * mm, "end": v(-80, 80) * mm});
            skLineSegment(sketch, "E79.8", {"start": v(60, 40.3) * mm, "end": v(60, -40.3) * mm});
            skArc(sketch, "E79.9", {"start": v(56.15, -48.18) * mm, "mid": v(58.99, -44.68) * mm, "end": v(60, -40.3) * mm});
            skArc(sketch, "E79.10", {"start": v(-56.15, -48.18) * mm, "mid": v(0, -67.5) * mm, "end": v(56.15, -48.18) * mm});
            skArc(sketch, "E79.11", {"start": v(-60, -40.3) * mm, "mid": v(-58.99, -44.68) * mm, "end": v(-56.15, -48.18) * mm});
            skLineSegment(sketch, "E79.12", {"start": v(-60, 40.3) * mm, "end": v(-60, -40.3) * mm});
            skArc(sketch, "E79.13", {"start": v(-56.15, 48.18) * mm, "mid": v(-58.99, 44.68) * mm, "end": v(-60, 40.3) * mm});
            skArc(sketch, "E79.14", {"start": v(56.15, 48.18) * mm, "mid": v(0, 67.5) * mm, "end": v(-56.15, 48.18) * mm});
            skArc(sketch, "E79.20", {"start": v(60, 40.3) * mm, "mid": v(58.99, 44.68) * mm, "end": v(56.15, 48.18) * mm});
            skCircle(sketch, "E79.24", {"center": v(60, 67.5) * mm, "radius": 4 * mm});
            skCircle(sketch, "E79.25", {"center": v(60, -67.5) * mm, "radius": 4 * mm});
            skCircle(sketch, "E79.26", {"center": v(-60, -67.5) * mm, "radius": 4 * mm});
            skCircle(sketch, "E79.27", {"center": v(-60, 67.5) * mm, "radius": 4 * mm});
            skLineSegment(sketch, "E80", {"start": v(0, 90) * mm, "end": v(0, 120) * mm, "construction": true});
            skPoint(sketch, "E80.endSnap0", {"position": v(0, 90) * mm});
            skCircle(sketch, "E81", {"center": v(0, 120) * mm, "radius": 6 * mm});
            skLineSegment(sketch, "E82", {"start": v(-15, 120) * mm, "end": v(-15, 108) * mm});
            skLineSegment(sketch, "E83", {"start": v(-15, 108) * mm, "end": v(-33, 90) * mm});
            skLineSegment(sketch, "E84", {"start": v(15, 120) * mm, "end": v(15, 108) * mm});
            skLineSegment(sketch, "E85", {"start": v(15, 108) * mm, "end": v(33, 90) * mm});
            skArc(sketch, "E86", {"start": v(15, 120) * mm, "mid": v(0, 135) * mm, "end": v(-15, 120) * mm});
            skLineSegment(sketch, "E87", {"start": v(-80, 0) * mm, "end": v(80, 0) * mm, "construction": true});
            skPoint(sketch, "E88.MirrorP", {"position": v(0, -90) * mm});
            skCircle(sketch, "E89.MirrorC", {"center": v(0, -120) * mm, "radius": 6 * mm});
            skLineSegment(sketch, "E90.MirrorCS", {"start": v(15, -120) * mm, "end": v(15, -108) * mm});
            skLineSegment(sketch, "E91.MirrorCS", {"start": v(-15, -120) * mm, "end": v(-15, -108) * mm});
            skArc(sketch, "E92.MirrorCS", {"start": v(15, -120) * mm, "mid": v(0, -135) * mm, "end": v(-15, -120) * mm});
            skLineSegment(sketch, "E93.MirrorCS", {"start": v(-15, -108) * mm, "end": v(-33, -90) * mm});
            skLineSegment(sketch, "E94.MirrorCS", {"start": v(15, -108) * mm, "end": v(33, -90) * mm});
            skLineSegment(sketch, "E95.MirrorCS", {"start": v(0, -90) * mm, "end": v(0, -120) * mm, "construction": true});
            skSolve(sketch);
        }
        {
            var Q0;
            Q0 = qSketchRegion(id + "F16", true);
            var Q1;
            Q1=makeQuery(id+"F2.opExtrude","CAP_FACE",FACE,{"disambiguationData":[OSD([sQuery(id+"F0.wireOp",EDGE,"E12"),sQuery(id+"F0.wireOp",EDGE,"E13"),sQuery(id+"F0.wireOp",EDGE,"E14"),sQuery(id+"F0.wireOp",EDGE,"E15"),sQuery(id+"F0.wireOp",EDGE,"E17.filletArc"),sQuery(id+"F0.wireOp",EDGE,"E18.filletArc"),sQuery(id+"F0.wireOp",EDGE,"E19.filletArc"),sQuery(id+"F0.wireOp",EDGE,"E20.filletArc"),sQuery(id+"F0.wireOp",EDGE,"E25.0"),sQuery(id+"F0.wireOp",EDGE,"E25.1"),sQuery(id+"F0.wireOp",EDGE,"E25.2"),sQuery(id+"F0.wireOp",EDGE,"E25.3"),sQuery(id+"F0.wireOp",EDGE,"E25.4"),sQuery(id+"F0.wireOp",EDGE,"E25.5"),sQuery(id+"F0.wireOp",EDGE,"E25.6"),sQuery(id+"F0.wireOp",EDGE,"E25.7")])],"isStart":false});
            extrude(context, id + "F17", {"entities" : qUnion([Q0]), "endBound" : BoundingType.UP_TO_SURFACE, "depth" : 25 * mm, "endBoundEntityFace" : qUnion([Q1]), "offsetDistance" : 25 * mm});
        }
    });
